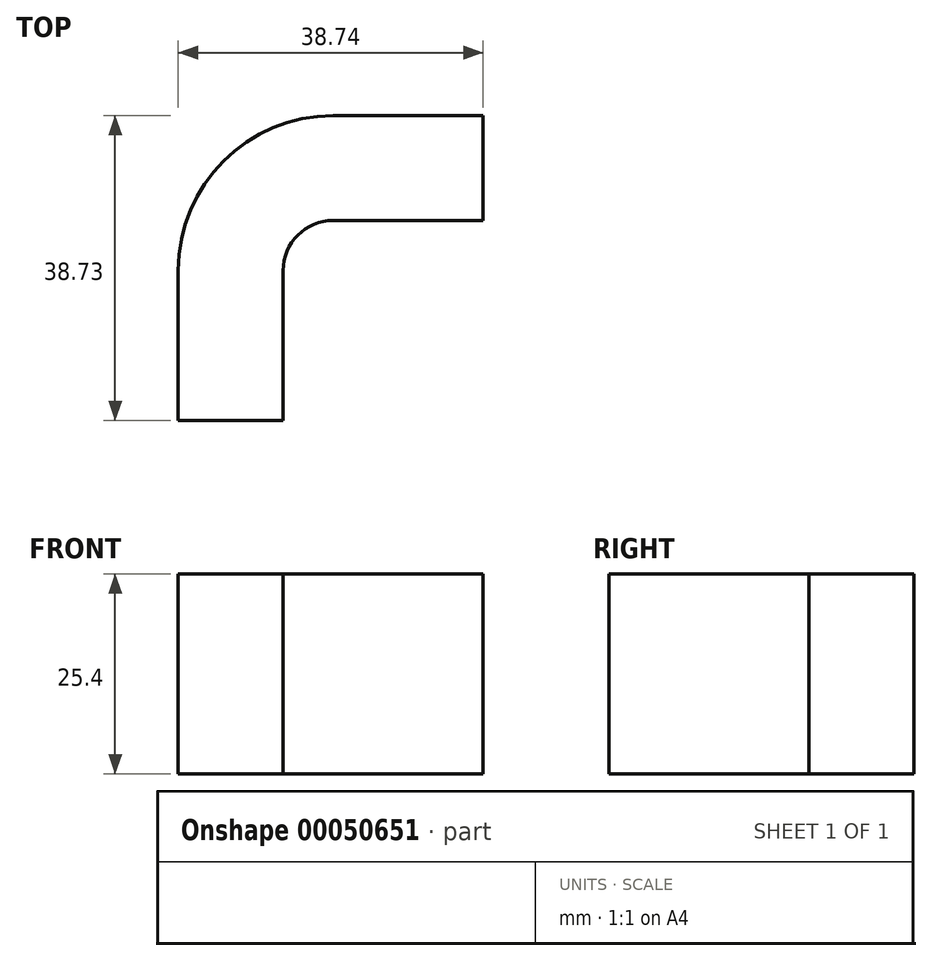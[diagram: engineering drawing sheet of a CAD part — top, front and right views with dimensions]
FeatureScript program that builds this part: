
annotation { "Feature Type Name" : "Feature", "Feature Type Description" : "" }
export const myFeature = defineFeature(function(context is Context, id is Id, definition is map)
    precondition{}
    {
        {
            var Q0;
            Q0=qCreatedBy(makeId("Top.planeOp"),FACE);
            var sketch = newSketch(context, id + "F0", { "sketchPlane" : qUnion([Q0])});
            skLineSegment(sketch, "E0", {"start": v(0, 0) * mm, "end": v(0, 19.05) * mm});
            skLineSegment(sketch, "E1", {"start": v(6.35, 25.4) * mm, "end": v(25.4, 25.4) * mm});
            skPoint(sketch, "E2.visualSharp", {"position": v(0, 25.4) * mm});
            skArc(sketch, "E2.filletArc", {"start": v(6.35, 25.4) * mm, "mid": v(1.86, 23.54) * mm, "end": v(0, 19.05) * mm});
            skLineSegment(sketch, "E3", {"start": v(0, 0) * mm, "end": v(-13.34, 0) * mm});
            skLineSegment(sketch, "E4", {"start": v(-13.34, 0) * mm, "end": v(-13.34, 19.05) * mm});
            skLineSegment(sketch, "E5", {"start": v(25.4, 25.4) * mm, "end": v(25.4, 38.74) * mm});
            skLineSegment(sketch, "E6", {"start": v(25.4, 38.74) * mm, "end": v(6.35, 38.74) * mm});
            skArc(sketch, "E7", {"start": v(6.35, 38.74) * mm, "mid": v(-7.57, 32.97) * mm, "end": v(-13.34, 19.05) * mm});
            skSolve(sketch);
        }
        {
            var Q0;
            Q0=qCreatedBy(makeId("Front.planeOp"),FACE);
            var sketch = newSketch(context, id + "F1", { "sketchPlane" : qUnion([Q0])});
            skCircle(sketch, "E8", {"center": v(0, 0) * mm, "radius": 13.34 * mm});
            skCircle(sketch, "E9", {"center": v(0, 0) * mm, "radius": 10.21 * mm});
            skSolve(sketch);
        }
        {
            var Q0;
            Q0=makeQuery(id+"F0.imprint","IMPRINT",FACE,{"disambiguationData":[TD([[makeQuery(id+"F0.imprint","IMPRINT",EDGE,{"derivedFrom":sQuery(id+"F0.wireOp",EDGE,"E0")}),1.0]])]});
            extrude(context, id + "F2", {"entities" : qUnion([Q0]), "depth" : 25.4 * mm});
        }
    });
